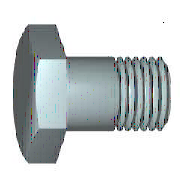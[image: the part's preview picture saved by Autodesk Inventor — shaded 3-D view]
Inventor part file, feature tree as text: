
AUTODESK INVENTOR PART (.ipt)
format: ipt  version: 2022 (Build 260153000, 153)  size: 195,072 bytes
history: native  units: mm (DEFAULTED — no unit token found)
features: sketch x3, extrude x1, chamfer x1, plane x1
ambient origin geometry x7: Origin, YZ Plane, XZ Plane, X Axis, Y Axis, Z Axis, Center Point
bodies: Solid1 (feature_tree), Body (feature_tree)
feature tree (6):
  extrude  "Head"  Depth=22.9mm
  chamfer  "Chamfer1"  Distance=2.4mm
  plane  "Work Plane1"
  sketch  "Sketch1"  dims[d0=25.0mm d1=22.9mm]
  sketch  "Sketch2"  dims[d2=4.0mm]
  sketch  "Sketch4"  dims[d12=90.0deg d3=2.4mm d4=0.0mm d5=30.0deg d21=90.0deg d6=0.429415mm d7=0.429515mm d8=0.0mm d9=0.4001mm d10=7.0mm d11=7.0mm d13=0.429515mm d14=4.0mm d15=22.9mm d16=0.0mm d19=7.0mm d55=45.0deg d57=0.0mm d58=0.0mm]
